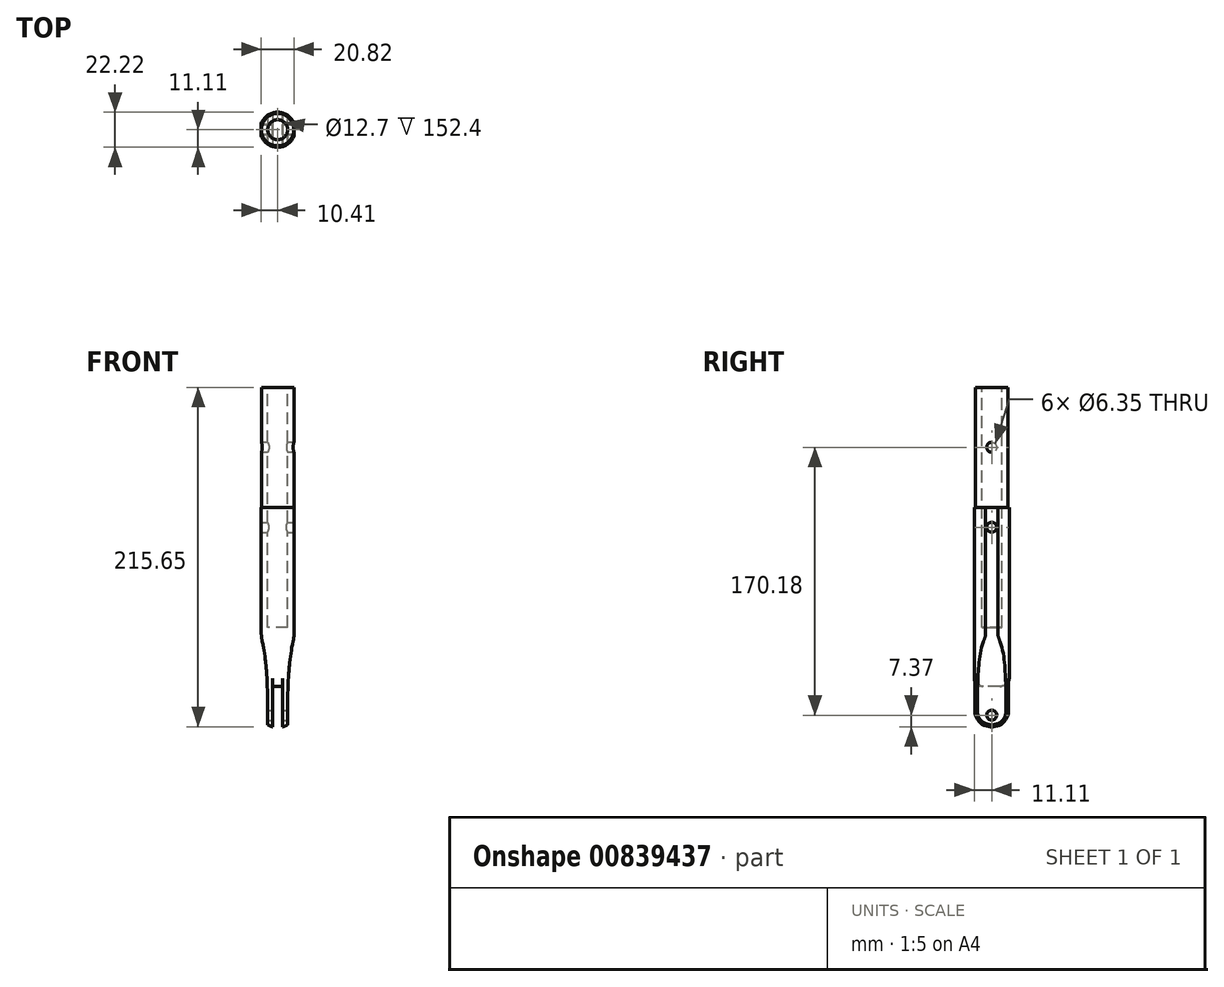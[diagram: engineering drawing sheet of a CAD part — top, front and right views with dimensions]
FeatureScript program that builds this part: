
annotation { "Feature Type Name" : "Feature", "Feature Type Description" : "" }
export const myFeature = defineFeature(function(context is Context, id is Id, definition is map)
    precondition{}
    {
        {
            var Q0;
            Q0=qCreatedBy(makeId("Top.planeOp"),FACE);
            var sketch = newSketch(context, id + "F0", { "sketchPlane" : qUnion([Q0])});
            skCircle(sketch, "E0", {"center": v(0, 0) * mm, "radius": 11.11 * mm});
            skSolve(sketch);
        }
        {
            var Q0;
            Q0=qSketchRegion(id+"F0",true);
            extrude(context, id + "F1", {"entities" : qUnion([Q0]), "depth" : 50.8 * mm, "offsetDistance" : 25.4 * mm});
        }
        {
            var Q0;
            Q0=makeQuery(id+"F1.opExtrude","CAP_FACE",FACE,{"disambiguationData":[OSD([sQuery(id+"F0.wireOp",EDGE,"E0")])],"isStart":true});
            var sketch = newSketch(context, id + "F2", { "sketchPlane" : qUnion([Q0])});
            skCircle(sketch, "E1", {"center": v(0, 0) * mm, "radius": 11.11 * mm});
            skSolve(sketch);
        }
        {
            var Q0;
            Q0=qSketchRegion(id+"F2",true);
            extrude(context, id + "F3", {"entities" : qUnion([Q0]), "operationType" : NewBodyOperationType.ADD, "depth" : 88.9 * mm, "offsetDistance" : 25.4 * mm});
        }
        {
            var Q0;
            Q0=qCreatedBy(makeId("Right.planeOp"),FACE);
            var sketch = newSketch(context, id + "F4", { "sketchPlane" : qUnion([Q0])});
            skCircle(sketch, "E2", {"center": v(0, 38.1) * mm, "radius": 3.18 * mm});
            skSolve(sketch);
        }
        {
            var Q0;
            Q0=qSketchRegion(id+"F4",true);
            extrude(context, id + "F5", {"entities" : qUnion([Q0]), "operationType" : NewBodyOperationType.REMOVE, "endBound" : BoundingType.THROUGH_ALL, "oppositeDirection" : true, "depth" : 25.4 * mm, "offsetDistance" : 25.4 * mm, "hasSecondDirection" : true, "secondDirectionBound" : BoundingType.THROUGH_ALL, "secondDirectionOppositeDirection" : false, "secondDirectionDepth" : 25.4 * mm});
        }
        {
            var Q0;
            Q0=qCreatedBy(makeId("Front.planeOp"),FACE);
            var sketch = newSketch(context, id + "F6", { "sketchPlane" : qUnion([Q0])});
            skLineSegment(sketch, "E3", {"start": v(0, -101.6) * mm, "end": v(3.18, -101.6) * mm, "construction": true});
            skLineSegment(sketch, "E4", {"start": v(0, -101.6) * mm, "end": v(-6.35, -101.6) * mm, "construction": true});
            skLineSegment(sketch, "E5.bottom", {"start": v(-6.35, -101.6) * mm, "end": v(-19.05, -101.6) * mm});
            skLineSegment(sketch, "E5.top", {"start": v(-6.35, -88.9) * mm, "end": v(-19.05, -88.9) * mm});
            skLineSegment(sketch, "E5.left", {"start": v(-6.35, -101.6) * mm, "end": v(-6.35, -88.9) * mm});
            skLineSegment(sketch, "E5.right", {"start": v(-19.05, -101.6) * mm, "end": v(-19.05, -88.9) * mm});
            skLineSegment(sketch, "E6.MirrorCS", {"start": v(6.35, -88.9) * mm, "end": v(19.05, -88.9) * mm});
            skLineSegment(sketch, "E7.MirrorCS", {"start": v(6.35, -101.6) * mm, "end": v(6.35, -88.9) * mm});
            skLineSegment(sketch, "E8.MirrorCS", {"start": v(6.35, -101.6) * mm, "end": v(19.05, -101.6) * mm});
            skLineSegment(sketch, "E9.MirrorCS", {"start": v(19.05, -101.6) * mm, "end": v(19.05, -88.9) * mm});
            skLineSegment(sketch, "E10", {"start": v(0, 0) * mm, "end": v(0, -25.4) * mm, "construction": true});
            skLineSegment(sketch, "E11", {"start": v(0, -25.4) * mm, "end": v(-12.7, -25.4) * mm, "construction": true});
            skLineSegment(sketch, "E12.MirrorCS", {"start": v(0, -25.4) * mm, "end": v(12.7, -25.4) * mm, "construction": true});
            skFitSpline(sketch, "E13", {"points": [v(-12.7, -25.4) * mm, v(-6.35, -88.9) * mm], "startDerivative": vector(18.42, -41.8) * mm, "endDerivative": vector(-0.74, -72.86) * mm});
            skFitSpline(sketch, "E14.MirrorCS", {"points": [v(12.7, -25.4) * mm, v(6.35, -88.9) * mm], "startDerivative": vector(-18.42, -41.8) * mm, "endDerivative": vector(0.74, -72.86) * mm});
            skLineSegment(sketch, "E15", {"start": v(-12.7, -25.4) * mm, "end": v(-19.05, -88.9) * mm});
            skLineSegment(sketch, "E16", {"start": v(12.7, -25.4) * mm, "end": v(19.05, -88.9) * mm});
            skSolve(sketch);
        }
        {
            var Q0;
            Q0=qSketchRegion(id+"F6",true);
            extrude(context, id + "F7", {"entities" : qUnion([Q0]), "operationType" : NewBodyOperationType.REMOVE, "endBound" : BoundingType.THROUGH_ALL, "oppositeDirection" : true, "depth" : 25.4 * mm, "offsetDistance" : 25.4 * mm, "hasSecondDirection" : true, "secondDirectionBound" : BoundingType.THROUGH_ALL, "secondDirectionOppositeDirection" : false, "secondDirectionDepth" : 25.4 * mm});
        }
        {
            var Q0;
            Q0=qCreatedBy(makeId("Right.planeOp"),FACE);
            var sketch = newSketch(context, id + "F8", { "sketchPlane" : qUnion([Q0])});
            skCircle(sketch, "E17", {"center": v(0, -81.28) * mm, "radius": 3.18 * mm});
            skSolve(sketch);
        }
        {
            var Q0;
            Q0=qSketchRegion(id+"F8",true);
            extrude(context, id + "F9", {"entities" : qUnion([Q0]), "operationType" : NewBodyOperationType.REMOVE, "endBound" : BoundingType.THROUGH_ALL, "oppositeDirection" : true, "depth" : 25.4 * mm, "offsetDistance" : 25.4 * mm, "hasSecondDirection" : true, "secondDirectionBound" : BoundingType.THROUGH_ALL, "secondDirectionOppositeDirection" : false, "secondDirectionDepth" : 25.4 * mm});
        }
        {
            var Q0;
            Q0=makeQuery(id+"F7.boolean.opBoolean","SPLIT",EDGE,{"disambiguationData":[OD(1.0)],"derivedFrom":makeQuery(id+"F3.opExtrude","CAP_EDGE",EDGE,{"disambiguationData":[OSD([sQuery(id+"F2.wireOp",EDGE,"E1")])],"isStart":false})});
            var Q1;
            Q1=makeQuery(id+"F7.boolean.opBoolean","SPLIT",EDGE,{"disambiguationData":[OD(0.0)],"derivedFrom":makeQuery(id+"F3.opExtrude","CAP_EDGE",EDGE,{"disambiguationData":[OSD([sQuery(id+"F2.wireOp",EDGE,"E1")])],"isStart":false})});
            fillet(context, id + "F10", {"entities" : qUnion([Q0, Q1]), "tangentPropagation" : true, "radius" : 10.16 * mm, "defaultsChanged" : true, "vertexSettings" : [], "allowEdgeOverflow" : false});
        }
        {
            var Q0;
            Q0=makeQuery(id+"F1.opExtrude","CAP_FACE",FACE,{"disambiguationData":[OSD([sQuery(id+"F0.wireOp",EDGE,"E0")])],"isStart":false});
            var sketch = newSketch(context, id + "F11", { "sketchPlane" : qUnion([Q0])});
            skCircle(sketch, "E18", {"center": v(0, 0) * mm, "radius": 6.35 * mm});
            skSolve(sketch);
        }
        {
            var Q0;
            Q0=qCreatedBy(makeId("Front.planeOp"),FACE);
            var sketch = newSketch(context, id + "F12", { "sketchPlane" : qUnion([Q0])});
            skLineSegment(sketch, "E19.bottom", {"start": v(3.18, -94.62) * mm, "end": v(-3.17, -94.62) * mm});
            skLineSegment(sketch, "E19.top", {"start": v(3.18, -62.87) * mm, "end": v(-3.17, -62.87) * mm});
            skLineSegment(sketch, "E19.left", {"start": v(3.18, -94.62) * mm, "end": v(3.18, -62.87) * mm});
            skLineSegment(sketch, "E19.right", {"start": v(-3.17, -94.62) * mm, "end": v(-3.17, -62.87) * mm});
            skPoint(sketch, "E19.middle", {"position": v(0, -78.74) * mm});
            skSolve(sketch);
        }
        {
            var Q0;
            Q0=qSketchRegion(id+"F12",true);
            extrude(context, id + "F13", {"entities" : qUnion([Q0]), "operationType" : NewBodyOperationType.REMOVE, "endBound" : BoundingType.THROUGH_ALL, "oppositeDirection" : true, "depth" : 25.4 * mm, "offsetDistance" : 25.4 * mm, "hasSecondDirection" : true, "secondDirectionBound" : BoundingType.THROUGH_ALL, "secondDirectionOppositeDirection" : false, "secondDirectionDepth" : 25.4 * mm});
        }
        {
            var Q0;
            Q0=makeQuery(id+"F13.boolean.opBoolean","INTERSECT",EDGE,{"disambiguationData":[OD(0.0)],"derivedFrom":[makeQuery(id+"F3.opExtrude","SWEPT_FACE",FACE,{"disambiguationData":[OSD([sQuery(id+"F2.wireOp",EDGE,"E1")])]}),makeQuery(id+"F13.opExtrude","SWEPT_FACE",FACE,{"disambiguationData":[OSD([sQuery(id+"F12.wireOp",EDGE,"E19.top")])]})]});
            var Q1;
            Q1=makeQuery(id+"F13.boolean.opBoolean","INTERSECT",EDGE,{"disambiguationData":[OD(1.0)],"derivedFrom":[makeQuery(id+"F3.opExtrude","SWEPT_FACE",FACE,{"disambiguationData":[OSD([sQuery(id+"F2.wireOp",EDGE,"E1")])]}),makeQuery(id+"F13.opExtrude","SWEPT_FACE",FACE,{"disambiguationData":[OSD([sQuery(id+"F12.wireOp",EDGE,"E19.top")])]})]});
            fillet(context, id + "F14", {"entities" : qUnion([Q0, Q1]), "tangentPropagation" : true, "radius" : 5.08 * mm, "defaultsChanged" : false, "vertexSettings" : [], "allowEdgeOverflow" : false});
        }
        {
            var Q0;
            Q0=makeQuery(id+"F1.opExtrude","CAP_FACE",FACE,{"disambiguationData":[OSD([sQuery(id+"F0.wireOp",EDGE,"E0")])],"isStart":false});
            var sketch = newSketch(context, id + "F15", { "sketchPlane" : qUnion([Q0])});
            skCircle(sketch, "E20", {"center": v(0, 0) * mm, "radius": 10.31 * mm});
            skSolve(sketch);
        }
        {
            var Q0;
            Q0 = qSketchRegion(id + "F15", true);
            extrude(context, id + "F16", {"entities" : qUnion([Q0]), "operationType" : NewBodyOperationType.ADD, "depth" : 76.2 * mm, "offsetDistance" : 25.4 * mm});
        }
        {
            var Q0;
            Q0=qCreatedBy(makeId("Right.planeOp"),FACE);
            var sketch = newSketch(context, id + "F17", { "sketchPlane" : qUnion([Q0])});
            skCircle(sketch, "E21", {"center": v(0, 88.9) * mm, "radius": 3.18 * mm});
            skSolve(sketch);
        }
        {
            var Q0;
            Q0 = qSketchRegion(id + "F17", true);
            extrude(context, id + "F18", {"entities" : qUnion([Q0]), "operationType" : NewBodyOperationType.REMOVE, "endBound" : BoundingType.THROUGH_ALL, "depth" : 25.4 * mm, "offsetDistance" : 25.4 * mm, "hasSecondDirection" : true, "secondDirectionOppositeDirection" : true, "secondDirectionDepth" : 25.4 * mm});
        }
        {
            var Q0;
            Q0=qSketchRegion(id+"F11",true);
            extrude(context, id + "F19", {"entities" : qUnion([Q0]), "operationType" : NewBodyOperationType.REMOVE, "oppositeDirection" : true, "depth" : 76.2 * mm, "offsetDistance" : 25.4 * mm, "hasSecondDirection" : true, "secondDirectionBound" : BoundingType.THROUGH_ALL, "secondDirectionOppositeDirection" : false, "secondDirectionDepth" : 25.4 * mm});
        }
        {
            var Q0;
            Q0=qCreatedBy(makeId("Front.planeOp"),FACE);
            var sketch = newSketch(context, id + "F20", { "sketchPlane" : qUnion([Q0])});
            skLineSegment(sketch, "E22", {"start": v(0, 0) * mm, "end": v(-10.41, 0) * mm, "construction": true});
            skLineSegment(sketch, "E23.MirrorCS", {"start": v(0, 0) * mm, "end": v(10.41, 0) * mm, "construction": true});
            skLineSegment(sketch, "E24.bottom", {"start": v(-10.41, -101.55) * mm, "end": v(-26.37, -101.55) * mm});
            skLineSegment(sketch, "E24.top", {"start": v(-10.41, 56.54) * mm, "end": v(-26.37, 56.54) * mm});
            skLineSegment(sketch, "E24.left", {"start": v(-10.41, -101.55) * mm, "end": v(-10.41, 56.54) * mm});
            skLineSegment(sketch, "E24.right", {"start": v(-26.37, -101.55) * mm, "end": v(-26.37, 56.54) * mm});
            skLineSegment(sketch, "E25.MirrorCS", {"start": v(10.41, 56.54) * mm, "end": v(26.37, 56.54) * mm});
            skLineSegment(sketch, "E26.MirrorCS", {"start": v(10.41, -101.55) * mm, "end": v(10.41, 56.54) * mm});
            skLineSegment(sketch, "E27.MirrorCS", {"start": v(26.37, -101.55) * mm, "end": v(26.37, 56.54) * mm});
            skLineSegment(sketch, "E28.MirrorCS", {"start": v(10.41, -101.55) * mm, "end": v(26.37, -101.55) * mm});
            skSolve(sketch);
        }
        {
            var Q0;
            Q0 = qSketchRegion(id + "F20", true);
            extrude(context, id + "F21", {"entities" : qUnion([Q0]), "operationType" : NewBodyOperationType.REMOVE, "oppositeDirection" : true, "depth" : 25.4 * mm, "offsetDistance" : 25.4 * mm, "hasSecondDirection" : true, "secondDirectionOppositeDirection" : false, "secondDirectionDepth" : 25.4 * mm});
        }
        {
            var Q0;
            Q0=makeQuery(id+"F21.boolean.opBoolean","INTERSECT",EDGE,{"derivedFrom":[makeQuery(id+"F7.boolean.opBoolean","COPY",FACE,{"derivedFrom":makeQuery(id+"F7.opExtrude","SWEPT_FACE",FACE,{"disambiguationData":[OSD([sQuery(id+"F6.wireOp",EDGE,"E13")])]})}),makeQuery(id+"F21.opExtrude","SWEPT_FACE",FACE,{"disambiguationData":[OSD([sQuery(id+"F20.wireOp",EDGE,"E24.left")])]})]});
            var Q1;
            Q1=makeQuery(id+"F21.boolean.opBoolean","INTERSECT",EDGE,{"derivedFrom":[makeQuery(id+"F7.boolean.opBoolean","COPY",FACE,{"derivedFrom":makeQuery(id+"F7.opExtrude","SWEPT_FACE",FACE,{"disambiguationData":[OSD([sQuery(id+"F6.wireOp",EDGE,"E14.MirrorCS")])]})}),makeQuery(id+"F21.opExtrude","SWEPT_FACE",FACE,{"disambiguationData":[OSD([sQuery(id+"F20.wireOp",EDGE,"E26.MirrorCS")])]})]});
            fillet(context, id + "F22", {"entities" : qUnion([Q0, Q1]), "tangentPropagation" : true, "radius" : 25.4 * mm, "defaultsChanged" : false, "vertexSettings" : [], "allowEdgeOverflow" : false});
        }
    });
